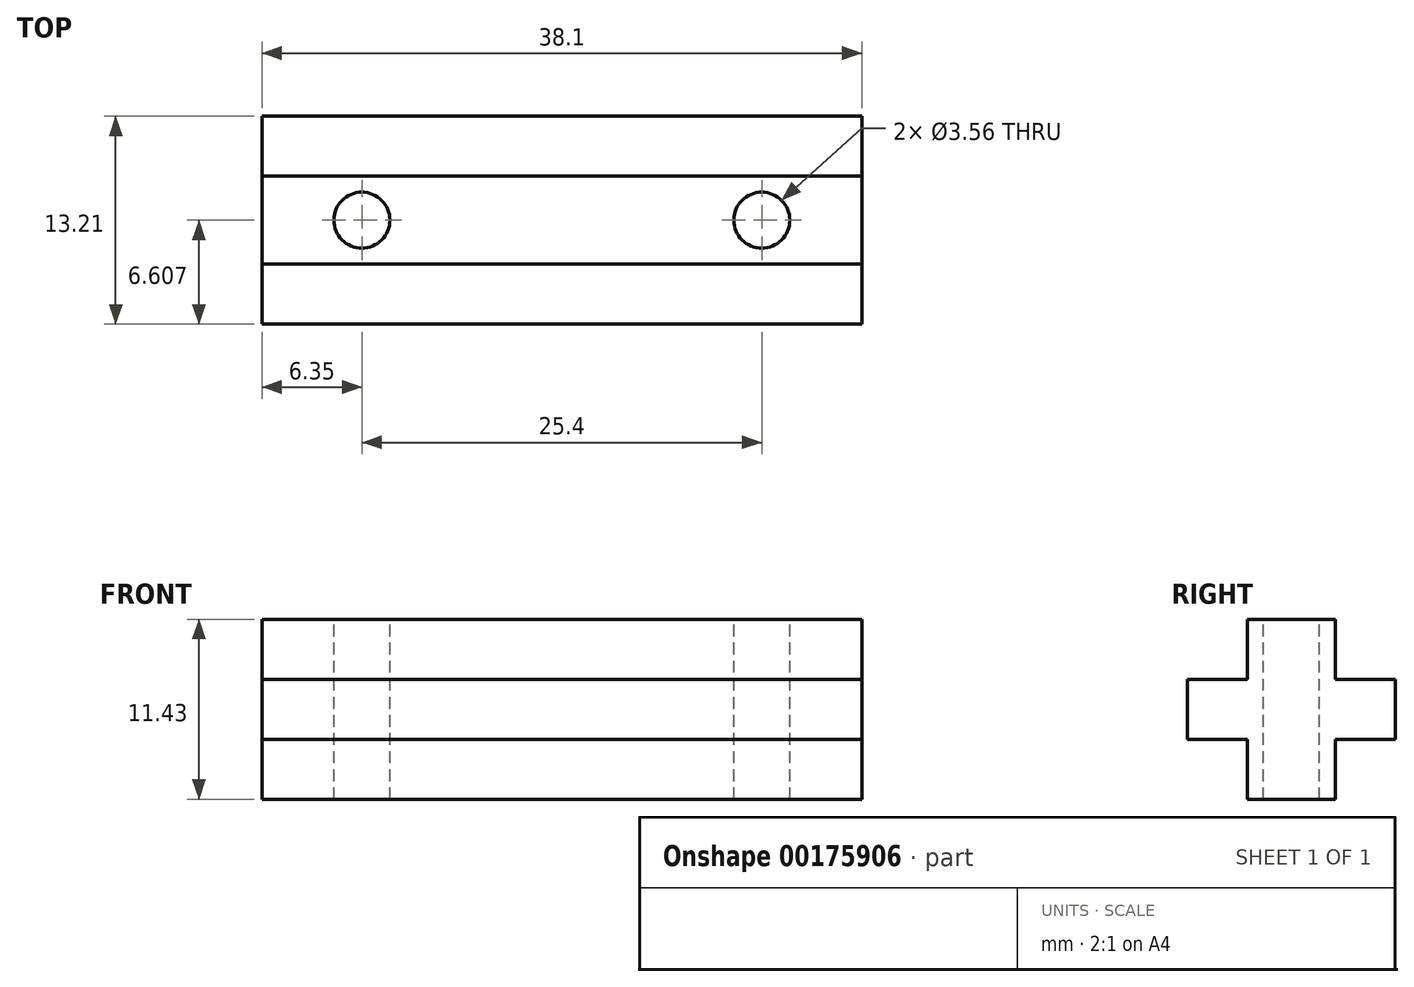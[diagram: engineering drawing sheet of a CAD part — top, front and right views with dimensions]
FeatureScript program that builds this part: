
annotation { "Feature Type Name" : "Feature", "Feature Type Description" : "" }
export const myFeature = defineFeature(function(context is Context, id is Id, definition is map)
    precondition{}
    {
        {
            var Q0;
            Q0=qCreatedBy(makeId("Right.planeOp"),FACE);
            var sketch = newSketch(context, id + "F0", { "sketchPlane" : qUnion([Q0])});
            skLineSegment(sketch, "E0", {"start": v(-1.2, -22.4) * mm, "end": v(4.38, -22.4) * mm});
            skLineSegment(sketch, "E1", {"start": v(4.38, -22.4) * mm, "end": v(4.38, -18.6) * mm});
            skLineSegment(sketch, "E2", {"start": v(4.38, -18.6) * mm, "end": v(8.2, -18.6) * mm});
            skLineSegment(sketch, "E3", {"start": v(8.2, -18.6) * mm, "end": v(8.2, -14.79) * mm});
            skLineSegment(sketch, "E4", {"start": v(8.2, -14.79) * mm, "end": v(4.38, -14.79) * mm});
            skLineSegment(sketch, "E5", {"start": v(4.38, -14.79) * mm, "end": v(4.38, -10.98) * mm});
            skLineSegment(sketch, "E6", {"start": v(4.38, -10.98) * mm, "end": v(-1.2, -10.98) * mm});
            skLineSegment(sketch, "E7", {"start": v(-1.2, -10.98) * mm, "end": v(-1.2, -14.79) * mm});
            skLineSegment(sketch, "E8", {"start": v(-1.2, -14.79) * mm, "end": v(-5.02, -14.79) * mm});
            skLineSegment(sketch, "E9", {"start": v(-5.02, -14.79) * mm, "end": v(-5.02, -18.6) * mm});
            skLineSegment(sketch, "E10", {"start": v(-5.02, -18.6) * mm, "end": v(-1.2, -18.6) * mm});
            skLineSegment(sketch, "E11", {"start": v(-1.2, -18.6) * mm, "end": v(-1.2, -22.4) * mm});
            skSolve(sketch);
        }
        {
            var Q0;
            Q0=makeQuery(id+"F0.imprint","IMPRINT",FACE,{"disambiguationData":[TD([[makeQuery(id+"F0.imprint","IMPRINT",EDGE,{"derivedFrom":sQuery(id+"F0.wireOp",EDGE,"E0")}),1.0]])]});
            extrude(context, id + "F1", {"entities" : qUnion([Q0]), "depth" : 38.1 * mm});
        }
        {
            var Q0;
            Q0=makeQuery(id+"F1.opExtrude","SWEPT_FACE",FACE,{"disambiguationData":[OSD([sQuery(id+"F0.wireOp",EDGE,"E6")])]});
            var sketch = newSketch(context, id + "F2", { "sketchPlane" : qUnion([Q0])});
            skCircle(sketch, "E12", {"center": v(6.35, 1.59) * mm, "radius": 1.78 * mm});
            skPoint(sketch, "E12.centerSnap0", {"position": v(0, 1.59) * mm});
            skCircle(sketch, "E13", {"center": v(31.75, 1.59) * mm, "radius": 1.78 * mm});
            skSolve(sketch);
        }
        {
            var Q0;
            Q0 = qSketchRegion(id + "F2", true);
            extrude(context, id + "F3", {"entities" : qUnion([Q0]), "operationType" : NewBodyOperationType.REMOVE, "oppositeDirection" : true, "depth" : 25.4 * mm});
        }
    });
